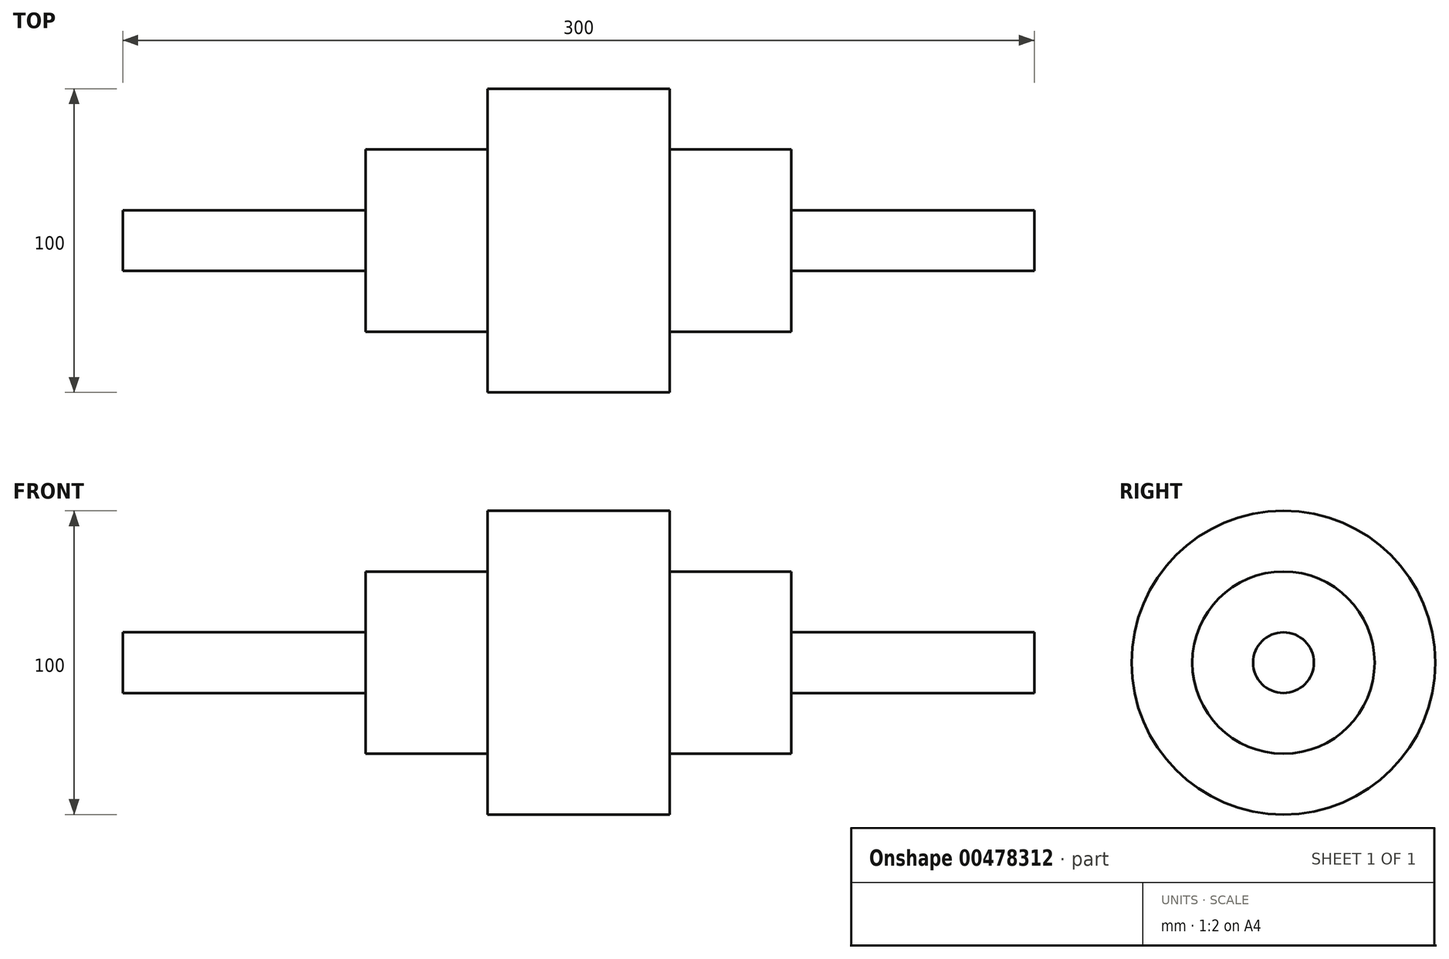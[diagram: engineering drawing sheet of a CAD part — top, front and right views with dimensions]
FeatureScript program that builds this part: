
annotation { "Feature Type Name" : "Feature", "Feature Type Description" : "" }
export const myFeature = defineFeature(function(context is Context, id is Id, definition is map)
    precondition{}
    {
        {
            var Q0;
            Q0=qCreatedBy(makeId("Front.planeOp"),FACE);
            var sketch = newSketch(context, id + "F0", { "sketchPlane" : qUnion([Q0])});
            skLineSegment(sketch, "E0", {"start": v(0, 0) * mm, "end": v(0, 10) * mm});
            skLineSegment(sketch, "E1", {"start": v(0, 10) * mm, "end": v(80, 10) * mm});
            skLineSegment(sketch, "E2", {"start": v(80, 10) * mm, "end": v(80, 30) * mm});
            skLineSegment(sketch, "E3", {"start": v(80, 30) * mm, "end": v(120, 30) * mm});
            skLineSegment(sketch, "E4", {"start": v(120, 30) * mm, "end": v(120, 50) * mm});
            skLineSegment(sketch, "E5", {"start": v(120, 50) * mm, "end": v(180, 50) * mm});
            skLineSegment(sketch, "E6", {"start": v(180, 50) * mm, "end": v(180, 30) * mm});
            skLineSegment(sketch, "E7", {"start": v(180, 30) * mm, "end": v(220, 30) * mm});
            skLineSegment(sketch, "E8", {"start": v(220, 30) * mm, "end": v(220, 10) * mm});
            skLineSegment(sketch, "E9", {"start": v(220, 10) * mm, "end": v(300, 10) * mm});
            skLineSegment(sketch, "E10", {"start": v(300, 10) * mm, "end": v(300, 0) * mm});
            skLineSegment(sketch, "E11", {"start": v(300, 0) * mm, "end": v(0, 0) * mm});
            skSolve(sketch);
        }
        {
            var Q0;
            Q0 = qSketchRegion(id + "F0", true);
            var Q1;
            Q1=sQuery(id+"F0.wireOp",EDGE,"E11");
            revolve(context, id + "F1", {"entities" : qUnion([Q0]), "axis" : qUnion([Q1]), "revolveType" : RevolveType.FULL});
        }
    });
